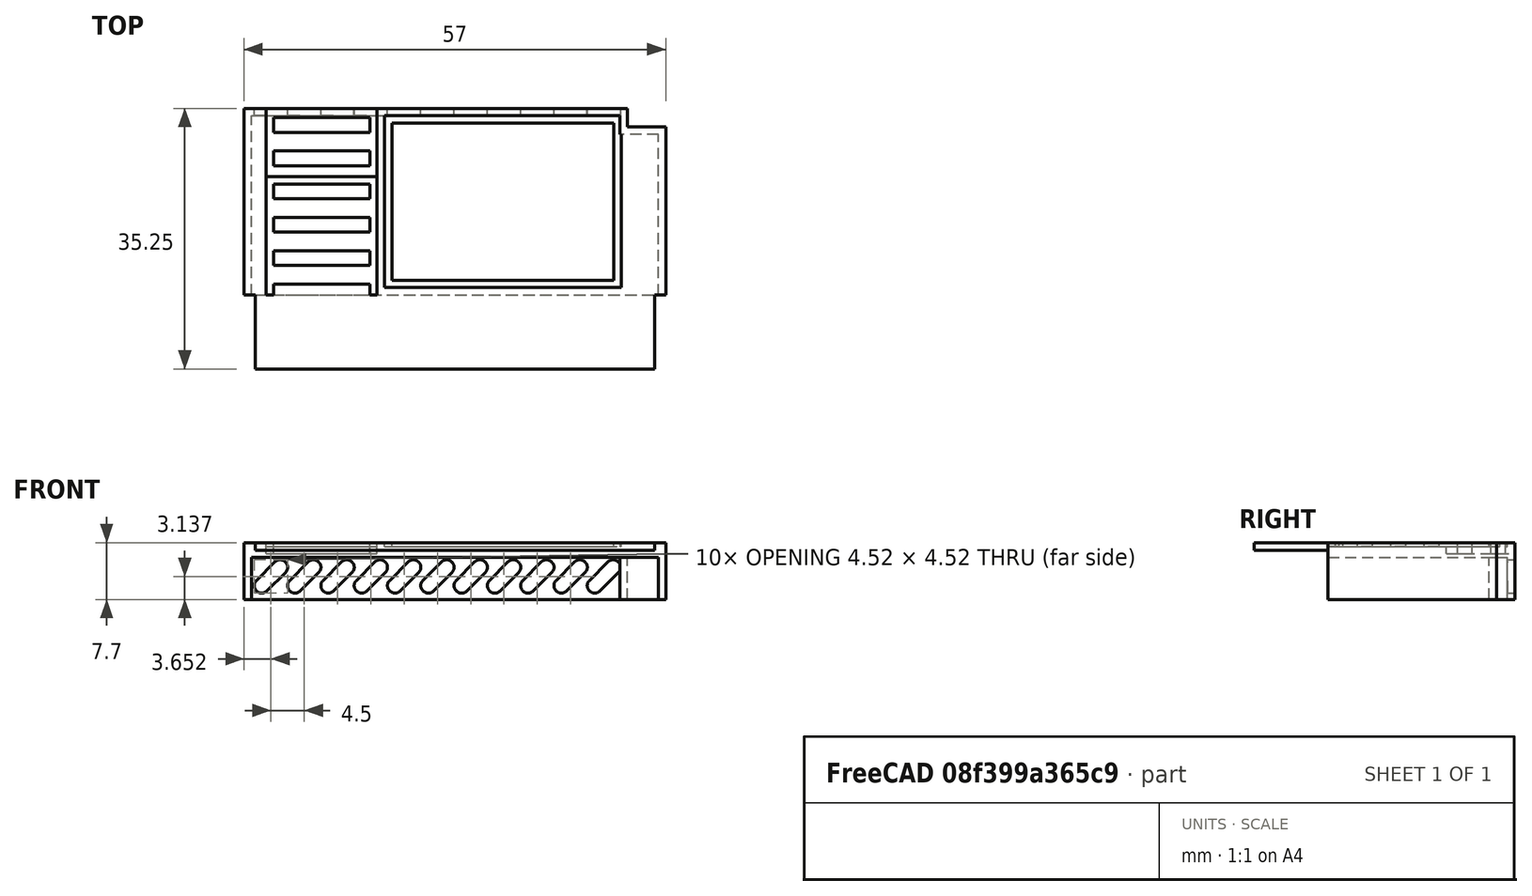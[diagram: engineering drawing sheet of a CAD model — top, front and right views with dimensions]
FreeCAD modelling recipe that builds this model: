
FCSTD DOCUMENT  (FreeCAD 0.19R24291 (Git))
Label: circuit_shield_cart_cover
License: All rights reserved
LicenseURL: http://en.wikipedia.org/wiki/All_rights_reserved
objects: Part::Box×29, Part::Fillet×11, Part::Cut×7, Part::MultiFuse×5
note: 52 computed .brp shape members not serialized (recipe doc carries the construction recipe); baked Part::Feature solids carry a one-line shape summary decoded from their .brp

FEATURE [Part::Box] Box007  label="Cube(top_cover_top_half)"
  AttacherType = Attacher::AttachEngine3D
  Height = 2
  Length = 57
  Placement = pos=(0,39,5.3) rot=(0,0,1;0rad)
  Width = 25.25
FEATURE [Part::Box] Box010  label="Cube(top_corner_cut)"
  AttacherType = Attacher::AttachEngine3D
  Height = 10
  Length = 10
  Placement = pos=(51.8,61.75,0) rot=(0,0,1;0rad)
  Width = 10
FEATURE [Part::Cut] Cut006
  Base = -> Box007
  Tool = -> Box010
FEATURE [Part::Box] Box017  label="Cube(game_lable_inner)"
  AttacherType = Attacher::AttachEngine3D
  Height = 0.5
  Length = 30
  Placement = pos=(20,41,6.8) rot=(0,0,1;0rad)
  Width = 21.25
FEATURE [Part::Box] Box018  label="Cube(cube_strips)"
  AttacherType = Attacher::AttachEngine3D
  Height = 0.5
  Length = 15
  Placement = pos=(3,39,6.8) rot=(0,0,1;0rad)
  Width = 16
FEATURE [Part::Box] Box019  label="Cube(cube_strip_top)"
  AttacherType = Attacher::AttachEngine3D
  Height = 1.5
  Length = 15
  Placement = pos=(3,55,5.8) rot=(0,0,1;0rad)
  Width = 9.25
FEATURE [Part::Box] Box029  label="Cube(cube_strip_top_outer)"
  AttacherType = Attacher::AttachEngine3D
  Height = 1.5
  Length = 17
  Placement = pos=(2,55,5.8) rot=(0,0,1;0rad)
  Width = 9.25
FEATURE [Part::MultiFuse] Fusion003
  Shapes = -> [Cut006,Box029]
FEATURE [Part::Cut] Cut008
  Base = -> Fusion003
  Tool = -> Box019
FEATURE [Part::Box] Box031  label="Cube(ladders)010"
  AttacherType = Attacher::AttachEngine3D
  Height = 1
  Length = 13
  Placement = pos=(4,39,6.3) rot=(0,0,1;0rad)
  Width = 1.5
FEATURE [Part::Box] Box032  label="Cube(ladders)011"
  AttacherType = Attacher::AttachEngine3D
  Height = 1
  Length = 13
  Placement = pos=(4,43,6.3) rot=(0,0,1;0rad)
  Width = 2
FEATURE [Part::Box] Box034  label="Cube(ladders)013"
  AttacherType = Attacher::AttachEngine3D
  Height = 1
  Length = 13
  Placement = pos=(4,47.5,6.3) rot=(0,0,1;0rad)
  Width = 2
FEATURE [Part::Box] Box035  label="Cube(ladders)014"
  AttacherType = Attacher::AttachEngine3D
  Height = 1
  Length = 13
  Placement = pos=(4,52,6.3) rot=(0,0,1;0rad)
  Width = 2
FEATURE [Part::Box] Box038  label="Cube(ladders)017"
  AttacherType = Attacher::AttachEngine3D
  Height = 1.5
  Length = 13
  Placement = pos=(4,56.5,5.8) rot=(0,0,1;0rad)
  Width = 2
FEATURE [Part::Box] Box040  label="Cube(ladders)019"
  AttacherType = Attacher::AttachEngine3D
  Height = 1.5
  Length = 13
  Placement = pos=(4,61,5.8) rot=(0,0,1;0rad)
  Width = 2
FEATURE [Part::Box] Box041  label="Cube(game_lable_outer)"
  AttacherType = Attacher::AttachEngine3D
  Height = 0.5
  Length = 32
  Placement = pos=(19,40,6.8) rot=(0,0,1;0rad)
  Width = 23.25
FEATURE [Part::MultiFuse] Fusion024
  Shapes = -> [Box040,Box038,Box035,Box034,Box032,Box031]
FEATURE [Part::Box] Box059  label="Cube002(cart_extender_thin)"
  AttacherType = Attacher::AttachEngine3D
  Height = 1
  Length = 54
  Placement = pos=(1.5,29,6.3) rot=(0,0,1;0rad)
  Width = 10
FEATURE [Part::Box] Box060  label="Cube002(back_fill_outer)"
  AttacherType = Attacher::AttachEngine3D
  Height = 5.7
  Length = 57
  Placement = pos=(0,39,-0.4) rot=(0,0,1;0rad)
  Width = 25.25
FEATURE [Part::Box] Box061  label="Cube002(back_fill_inner)"
  AttacherType = Attacher::AttachEngine3D
  Height = 5.7
  Length = 55
  Placement = pos=(1,39,-0.4) rot=(0,0,1;0rad)
  Width = 24.25
FEATURE [Part::Box] Box062  label="Cube002(back_fill_outer_corner)"
  AttacherType = Attacher::AttachEngine3D
  Height = 7.7
  Length = 5.2
  Placement = pos=(51.8,61.75,-0.4) rot=(0,0,1;0rad)
  Width = 2.5
FEATURE [Part::Box] Box063  label="Cube002(back_fill_inner)_corner)"
  AttacherType = Attacher::AttachEngine3D
  Height = 7.7
  Length = 6.2
  Placement = pos=(50.8,60.75,-0.4) rot=(0,0,1;0rad)
  Width = 3.5
FEATURE [Part::Cut] Cut021
  Base = -> Box060
  Tool = -> Box061
FEATURE [Part::MultiFuse] Fusion025
  Shapes = -> [Box063,Cut021]
FEATURE [Part::Cut] Cut022
  Base = -> Fusion025
  Tool = -> Box062
FEATURE [Part::Cut] Cut023
  Base = -> Cut008
  Tool = -> Box018
FEATURE [Part::Cut] Cut024
  Base = -> Cut023
  Tool = -> Box041
FEATURE [Part::Box] Box064  label="Cube002(top_grill)"
  AttacherType = Attacher::AttachEngine3D
  Height = 5.5
  Length = 2
  Placement = pos=(1,63.25,1.5) rot=(0,1,0;0.785398rad)
  Width = 1
FEATURE [Part::Fillet] Fillet
  Base = -> Box064
  Edges = 4 edges r=0.95: [Edge2,Edge4,Edge6,Edge8]
FEATURE [Part::Box] Box065  label="Cube002(top_grill)001"
  AttacherType = Attacher::AttachEngine3D
  Height = 5.5
  Length = 2
  Placement = pos=(5.5,63.25,1.5) rot=(0,1,0;0.785398rad)
  Width = 1
FEATURE [Part::Fillet] Fillet001
  Base = -> Box065
  Edges = 4 edges r=0.95: [Edge2,Edge4,Edge6,Edge8]
FEATURE [Part::MultiFuse] Fusion027
  Shapes = -> [Fusion024,Box059,Cut024,Cut022,Box017]
FEATURE [Part::Box] Box066  label="Cube002(top_grill)002"
  AttacherType = Attacher::AttachEngine3D
  Height = 5.5
  Length = 2
  Placement = pos=(10,63.25,1.5) rot=(0,1,0;0.785398rad)
  Width = 1
FEATURE [Part::Fillet] Fillet002
  Base = -> Box066
  Edges = 4 edges r=0.95: [Edge2,Edge4,Edge6,Edge8]
FEATURE [Part::Box] Box067  label="Cube002(top_grill)003"
  AttacherType = Attacher::AttachEngine3D
  Height = 5.5
  Length = 2
  Placement = pos=(14.5,63.25,1.5) rot=(0,1,0;0.785398rad)
  Width = 1
FEATURE [Part::Fillet] Fillet003
  Base = -> Box067
  Edges = 4 edges r=0.95: [Edge2,Edge4,Edge6,Edge8]
FEATURE [Part::Box] Box068  label="Cube002(top_grill)004"
  AttacherType = Attacher::AttachEngine3D
  Height = 5.5
  Length = 2
  Placement = pos=(19,63.25,1.5) rot=(0,1,0;0.785398rad)
  Width = 1
FEATURE [Part::Fillet] Fillet004
  Base = -> Box068
  Edges = 4 edges r=0.95: [Edge2,Edge4,Edge6,Edge8]
FEATURE [Part::Box] Box069  label="Cube002(top_grill)005"
  AttacherType = Attacher::AttachEngine3D
  Height = 5.5
  Length = 2
  Placement = pos=(23.5,63.25,1.5) rot=(0,1,0;0.785398rad)
  Width = 1
FEATURE [Part::Fillet] Fillet005
  Base = -> Box069
  Edges = 4 edges r=0.95: [Edge2,Edge4,Edge6,Edge8]
FEATURE [Part::Box] Box070  label="Cube002(top_grill)006"
  AttacherType = Attacher::AttachEngine3D
  Height = 5.5
  Length = 2
  Placement = pos=(28,63.25,1.5) rot=(0,1,0;0.785398rad)
  Width = 1
FEATURE [Part::Fillet] Fillet006
  Base = -> Box070
  Edges = 4 edges r=0.95: [Edge2,Edge4,Edge6,Edge8]
FEATURE [Part::Box] Box071  label="Cube002(top_grill)007"
  AttacherType = Attacher::AttachEngine3D
  Height = 5.5
  Length = 2
  Placement = pos=(32.5,63.25,1.5) rot=(0,1,0;0.785398rad)
  Width = 1
FEATURE [Part::Fillet] Fillet007
  Base = -> Box071
  Edges = 4 edges r=0.95: [Edge2,Edge4,Edge6,Edge8]
FEATURE [Part::Box] Box072  label="Cube002(top_grill)008"
  AttacherType = Attacher::AttachEngine3D
  Height = 5.5
  Length = 2
  Placement = pos=(37,63.25,1.5) rot=(0,1,0;0.785398rad)
  Width = 1
FEATURE [Part::Fillet] Fillet008
  Base = -> Box072
  Edges = 4 edges r=0.95: [Edge2,Edge4,Edge6,Edge8]
FEATURE [Part::Box] Box073  label="Cube002(top_grill)009"
  AttacherType = Attacher::AttachEngine3D
  Height = 5.5
  Length = 2
  Placement = pos=(41.5,63.25,1.5) rot=(0,1,0;0.785398rad)
  Width = 1
FEATURE [Part::Fillet] Fillet009
  Base = -> Box073
  Edges = 4 edges r=0.95: [Edge2,Edge4,Edge6,Edge8]
FEATURE [Part::Box] Box074  label="Cube002(top_grill)010"
  AttacherType = Attacher::AttachEngine3D
  Height = 5.5
  Length = 2
  Placement = pos=(46,63.25,1.5) rot=(0,1,0;0.785398rad)
  Width = 1
FEATURE [Part::Fillet] Fillet010
  Base = -> Box074
  Edges = 4 edges r=0.95: [Edge2,Edge4,Edge6,Edge8]
FEATURE [Part::MultiFuse] Fusion028
  Shapes = -> [Fillet,Fillet001,Fillet002,Fillet003,Fillet004,Fillet005,Fillet006,Fillet007,Fillet008,Fillet009,Fillet010]
FEATURE [Part::Cut] Cut025
  Base = -> Fusion027
  Tool = -> Fusion028
